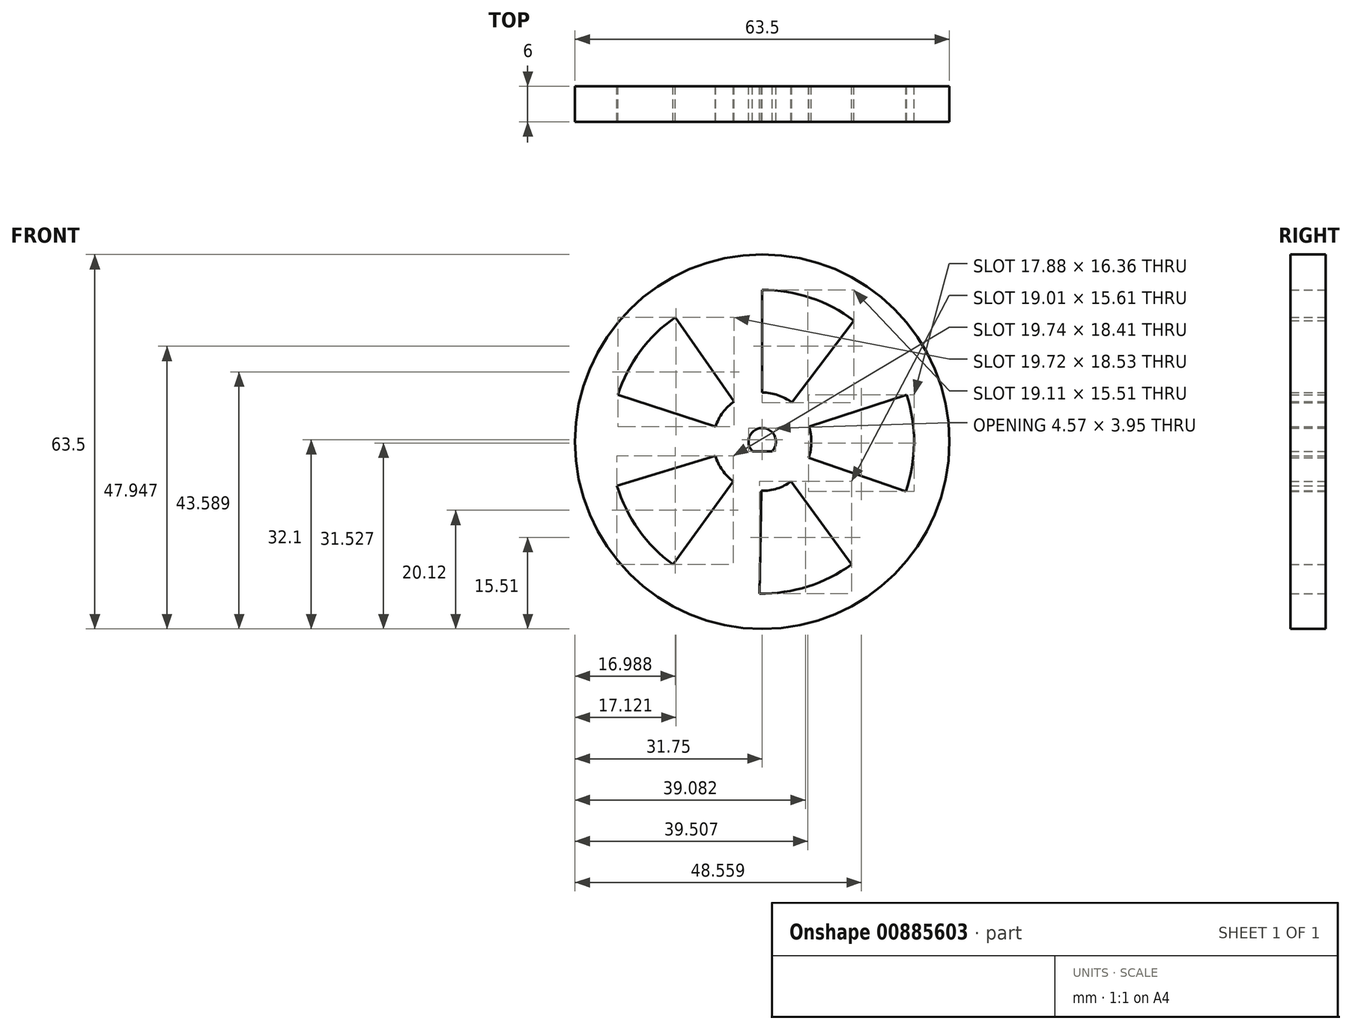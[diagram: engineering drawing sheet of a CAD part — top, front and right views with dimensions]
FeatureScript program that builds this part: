
annotation { "Feature Type Name" : "Feature", "Feature Type Description" : "" }
export const myFeature = defineFeature(function(context is Context, id is Id, definition is map)
    precondition{}
    {
        {
            var Q0;
            Q0=qCreatedBy(makeId("Front.planeOp"),FACE);
            var sketch = newSketch(context, id + "F0", { "sketchPlane" : qUnion([Q0])});
            skCircle(sketch, "E0", {"center": v(0, 0) * mm, "radius": 31.75 * mm});
            skArc(sketch, "E1", {"start": v(1.68, -1.67) * mm, "mid": v(0, 2.38) * mm, "end": v(-1.68, -1.68) * mm});
            skLineSegment(sketch, "E2", {"start": v(0, 2.38) * mm, "end": v(0, -1.68) * mm, "construction": true});
            skLineSegment(sketch, "E3", {"start": v(-1.68, -1.68) * mm, "end": v(1.68, -1.68) * mm});
            skArc(sketch, "E4.0", {"start": v(1.66, -1.62) * mm, "mid": v(0, 2.33) * mm, "end": v(-1.66, -1.63) * mm});
            skLineSegment(sketch, "E4.1", {"start": v(-1.66, -1.62) * mm, "end": v(1.66, -1.62) * mm});
            skCircle(sketch, "E5", {"center": v(0, 0) * mm, "radius": 8.32 * mm});
            skCircle(sketch, "E6", {"center": v(0, 0) * mm, "radius": 25.75 * mm});
            skLineSegment(sketch, "E7", {"start": v(-4.77, 6.82) * mm, "end": v(-14.75, 21.1) * mm});
            skLineSegment(sketch, "E8", {"start": v(0, 8.32) * mm, "end": v(0, 25.75) * mm});
            skLineSegment(sketch, "E9.1.0", {"start": v(-7.96, -2.43) * mm, "end": v(-24.63, -7.5) * mm});
            skLineSegment(sketch, "E9.1.1", {"start": v(-7.92, 2.57) * mm, "end": v(-24.49, 7.96) * mm});
            skLineSegment(sketch, "E9.2.0", {"start": v(-0.15, -8.32) * mm, "end": v(-0.47, -25.75) * mm});
            skLineSegment(sketch, "E9.2.1", {"start": v(-4.9, -6.74) * mm, "end": v(-15.14, -20.83) * mm});
            skLineSegment(sketch, "E9.3.0", {"start": v(7.87, -2.72) * mm, "end": v(24.34, -8.4) * mm});
            skLineSegment(sketch, "E9.3.1", {"start": v(4.9, -6.74) * mm, "end": v(15.14, -20.83) * mm});
            skLineSegment(sketch, "E9.4.0", {"start": v(5.02, 6.64) * mm, "end": v(15.51, 20.55) * mm});
            skLineSegment(sketch, "E9.4.1", {"start": v(7.92, 2.57) * mm, "end": v(24.49, 7.96) * mm});
            skSolve(sketch);
        }
        {
            var Q0;
            Q0 = qSketchRegion(id + "F0", true);
            var Q1;
            {var subQ0=sQuery(id+"F0.wireOp",EDGE,"E7");Q1=makeQuery(id+"F0.imprint","IMPRINT",FACE,{"disambiguationData":[TD([[makeQuery(id+"F0.imprint","IMPRINT",EDGE,{"derivedFrom":subQ0}),-1.0]])]});}
            var Q2;
            {var subQ0=sQuery(id+"F0.wireOp",EDGE,"E9.4.0");Q2=makeQuery(id+"F0.imprint","IMPRINT",FACE,{"disambiguationData":[TD([[makeQuery(id+"F0.imprint","IMPRINT",EDGE,{"derivedFrom":subQ0}),-1.0]])]});}
            var Q3;
            {var subQ0=sQuery(id+"F0.wireOp",EDGE,"E9.3.0");Q3=makeQuery(id+"F0.imprint","IMPRINT",FACE,{"disambiguationData":[TD([[makeQuery(id+"F0.imprint","IMPRINT",EDGE,{"derivedFrom":subQ0}),-1.0]])]});}
            var Q4;
            {var subQ0=sQuery(id+"F0.wireOp",EDGE,"E9.2.0");Q4=makeQuery(id+"F0.imprint","IMPRINT",FACE,{"disambiguationData":[TD([[makeQuery(id+"F0.imprint","IMPRINT",EDGE,{"derivedFrom":subQ0}),-1.0]])]});}
            var Q5;
            {var subQ0=sQuery(id+"F0.wireOp",EDGE,"E9.1.0");Q5=makeQuery(id+"F0.imprint","IMPRINT",FACE,{"disambiguationData":[TD([[makeQuery(id+"F0.imprint","IMPRINT",EDGE,{"derivedFrom":subQ0}),-1.0]])]});}
            var Q6;
            Q6=makeQuery(id+"F0.imprint","IMPRINT",FACE,{"disambiguationData":[TD([[makeQuery(id+"F0.imprint","IMPRINT",EDGE,{"derivedFrom":sQuery(id+"F0.wireOp",EDGE,"E1")}),-1.0]])]});
            var Q7;
            Q7=makeQuery(id+"F0.imprint","IMPRINT",FACE,{"disambiguationData":[TD([[makeQuery(id+"F0.imprint","IMPRINT",EDGE,{"derivedFrom":sQuery(id+"F0.wireOp",EDGE,"E1")}),1.0]])]});
            extrude(context, id + "F1", {"entities" : qUnion([Q0, Q1, Q2, Q3, Q4, Q5, Q6, Q7]), "depth" : 6 * mm, "offsetDistance" : 25 * mm});
        }
    });
